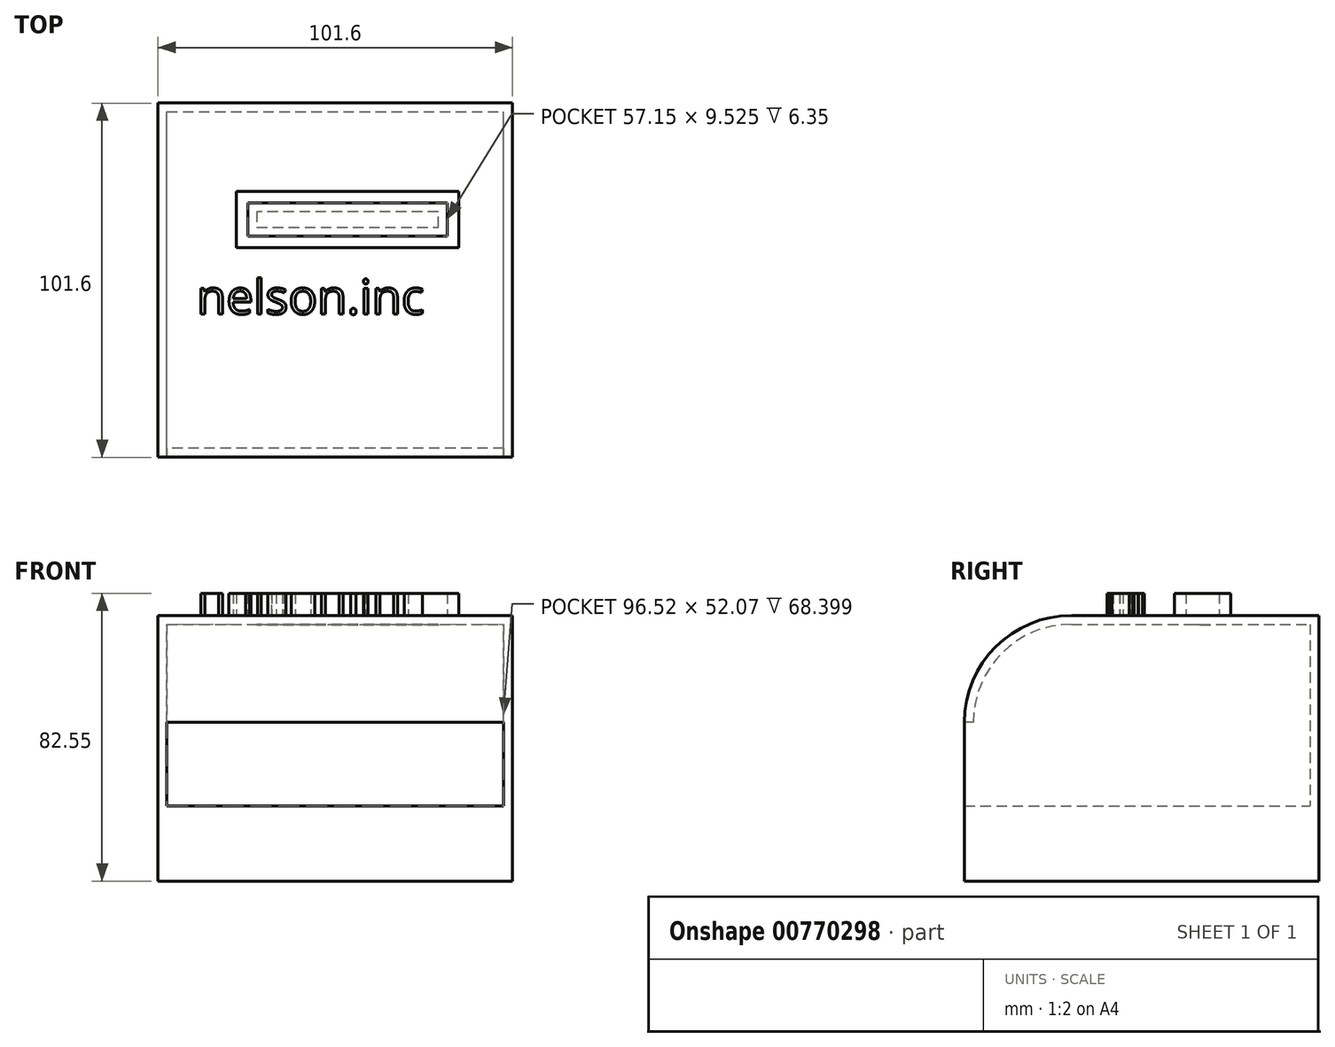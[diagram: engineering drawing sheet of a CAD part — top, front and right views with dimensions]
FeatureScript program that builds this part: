
annotation { "Feature Type Name" : "Feature", "Feature Type Description" : "" }
export const myFeature = defineFeature(function(context is Context, id is Id, definition is map)
    precondition{}
    {
        {
            var Q0;
            Q0=qCreatedBy(makeId("Top.planeOp"),FACE);
            var sketch = newSketch(context, id + "F0", { "sketchPlane" : qUnion([Q0])});
            skLineSegment(sketch, "E0.bottom", {"start": v(-76.75, -73.57) * mm, "end": v(24.85, -73.57) * mm});
            skLineSegment(sketch, "E0.top", {"start": v(-76.75, 28.03) * mm, "end": v(24.85, 28.03) * mm});
            skLineSegment(sketch, "E0.left", {"start": v(-76.75, -73.57) * mm, "end": v(-76.75, 28.03) * mm});
            skLineSegment(sketch, "E0.right", {"start": v(24.85, -73.57) * mm, "end": v(24.85, 28.03) * mm});
            skSolve(sketch);
        }
        {
            var Q0;
            Q0=makeQuery(id+"F0.imprint","IMPRINT",FACE,{"disambiguationData":[TD([[makeQuery(id+"F0.imprint","IMPRINT",EDGE,{"derivedFrom":sQuery(id+"F0.wireOp",EDGE,"E0.bottom")}),1.0]])]});
            extrude(context, id + "F1", {"entities" : qUnion([Q0]), "depth" : 76.2 * mm, "offsetDistance" : 25.4 * mm});
        }
        {
            var Q0;
            Q0=makeQuery(id+"F1.opExtrude","CAP_EDGE",EDGE,{"disambiguationData":[OSD([sQuery(id+"F0.wireOp",EDGE,"E0.bottom")])],"isStart":false});
            fillet(context, id + "F2", {"entities" : qUnion([Q0]), "radius" : 30.66 * mm, "tangentPropagation" : true, "allowEdgeOverflow" : false});
        }
        {
            var Q0;
            Q0=makeQuery(id+"F1.opExtrude","SWEPT_FACE",FACE,{"disambiguationData":[OSD([sQuery(id+"F0.wireOp",EDGE,"E0.bottom")])]});
            shell(context, id + "F3", {"entities" : qUnion([Q0]), "thickness" : 2.54 * mm});
        }
        {
            var Q0;
            Q0=makeQuery(id+"F1.opExtrude","CAP_FACE",FACE,{"disambiguationData":[OSD([sQuery(id+"F0.wireOp",EDGE,"E0.bottom"),sQuery(id+"F0.wireOp",EDGE,"E0.top"),sQuery(id+"F0.wireOp",EDGE,"E0.left"),sQuery(id+"F0.wireOp",EDGE,"E0.right")])],"isStart":false});
            var sketch = newSketch(context, id + "F4", { "sketchPlane" : qUnion([Q0])});
            skLineSegment(sketch, "E1.bottom", {"start": v(-51.02, -0.56) * mm, "end": v(6.13, -0.56) * mm});
            skLineSegment(sketch, "E1.top", {"start": v(-51.02, -10.09) * mm, "end": v(6.13, -10.09) * mm});
            skLineSegment(sketch, "E1.left", {"start": v(-51.02, -0.56) * mm, "end": v(-51.02, -10.09) * mm});
            skLineSegment(sketch, "E1.right", {"start": v(6.13, -0.56) * mm, "end": v(6.13, -10.09) * mm});
            skSolve(sketch);
        }
        {
            var Q0;
            Q0=makeQuery(id+"F4.imprint","IMPRINT",FACE,{"disambiguationData":[TD([[makeQuery(id+"F4.imprint","IMPRINT",EDGE,{"derivedFrom":sQuery(id+"F4.wireOp",EDGE,"E1.bottom")}),-1.0]])]});
            var sketch = newSketch(context, id + "F5", { "sketchPlane" : qUnion([Q0])});
            skLineSegment(sketch, "E2.0", {"start": v(-54.32, 2.74) * mm, "end": v(-54.32, -13.39) * mm});
            skLineSegment(sketch, "E2.1", {"start": v(9.44, 2.74) * mm, "end": v(-54.32, 2.74) * mm});
            skLineSegment(sketch, "E2.2", {"start": v(9.44, -13.39) * mm, "end": v(9.44, 2.74) * mm});
            skLineSegment(sketch, "E2.3", {"start": v(-54.32, -13.39) * mm, "end": v(9.44, -13.39) * mm});
            skSolve(sketch);
        }
        {
            var Q0;
            Q0=makeQuery(id+"F5.imprint","IMPRINT",FACE,{"disambiguationData":[TD([[makeQuery(id+"F5.imprint","IMPRINT",EDGE,{"derivedFrom":sQuery(id+"F5.wireOp",EDGE,"E2.0")}),1.0]])]});
            extrude(context, id + "F6", {"entities" : qUnion([Q0]), "operationType" : NewBodyOperationType.ADD, "depth" : 6.35 * mm, "offsetDistance" : 25.4 * mm});
        }
        {
            var Q0;
            Q0=makeQuery(id+"F4.imprint","IMPRINT",FACE,{"disambiguationData":[TD([[makeQuery(id+"F4.imprint","IMPRINT",EDGE,{"derivedFrom":sQuery(id+"F4.wireOp",EDGE,"E1.bottom")}),1.0]])]});
            var sketch = newSketch(context, id + "F7", { "sketchPlane" : qUnion([Q0])});
            skText(sketch, "E3", { "text": "nelson.inc\n", "fontName": "OpenSans-Regular.ttf"});
            const initialGuessF7  = {"E3": [-0.06564, -0.03249, 1, 0, 0.00992]};
            skSetInitialGuess(sketch, initialGuessF7);
            skSolve(sketch);
        }
        {
            var Q0;
            Q0 = qSketchRegion(id + "F7", true);
            extrude(context, id + "F8", {"entities" : qUnion([Q0]), "operationType" : NewBodyOperationType.ADD, "depth" : 6.35 * mm, "offsetDistance" : 25.4 * mm});
        }
        {
            var Q0;
            Q0=makeQuery(id+"F4.imprint","IMPRINT",FACE,{"disambiguationData":[TD([[makeQuery(id+"F4.imprint","IMPRINT",EDGE,{"derivedFrom":sQuery(id+"F4.wireOp",EDGE,"E1.bottom")}),-1.0]])]});
            var sketch = newSketch(context, id + "F9", { "sketchPlane" : qUnion([Q0])});
            skLineSegment(sketch, "E4.0", {"start": v(-48.48, -3.1) * mm, "end": v(-48.48, -7.55) * mm});
            skLineSegment(sketch, "E4.1", {"start": v(3.6, -3.1) * mm, "end": v(-48.48, -3.1) * mm});
            skLineSegment(sketch, "E4.2", {"start": v(3.6, -7.55) * mm, "end": v(3.6, -3.1) * mm});
            skLineSegment(sketch, "E4.3", {"start": v(-48.48, -7.55) * mm, "end": v(3.6, -7.55) * mm});
            skSolve(sketch);
        }
        {
            var Q0;
            Q0=makeQuery(id+"F9.imprint","IMPRINT",FACE,{"disambiguationData":[TD([[makeQuery(id+"F9.imprint","IMPRINT",EDGE,{"derivedFrom":sQuery(id+"F9.wireOp",EDGE,"E4.0")}),1.0]])]});
            extrude(context, id + "F10", {"entities" : qUnion([Q0]), "operationType" : NewBodyOperationType.ADD, "oppositeDirection" : true, "depth" : 2.8 * mm, "offsetDistance" : 25.4 * mm});
        }
        {
            var Q0;
            {var subQ0=sQuery(id+"F0.wireOp",EDGE,"E0.right");var subQ1=sQuery(id+"F0.wireOp",EDGE,"E0.left");var subQ2=sQuery(id+"F0.wireOp",EDGE,"E0.top");var subQ3=sQuery(id+"F0.wireOp",EDGE,"E0.bottom");Q0=makeQuery(id+"F3.opShell","OFFSET_FACE",FACE,{"disambiguationData":[OSD([subQ3,subQ2,subQ1,subQ0]),TDD([makeQuery(id+"F1.opExtrude","CAP_FACE",FACE,{"disambiguationData":[OSD([subQ3,subQ2,subQ1,subQ0])],"isStart":true})])]});}
            extrude(context, id + "F11", {"entities" : qUnion([Q0]), "operationType" : NewBodyOperationType.ADD, "depth" : 19.05 * mm, "offsetDistance" : 25.4 * mm});
        }
    });
